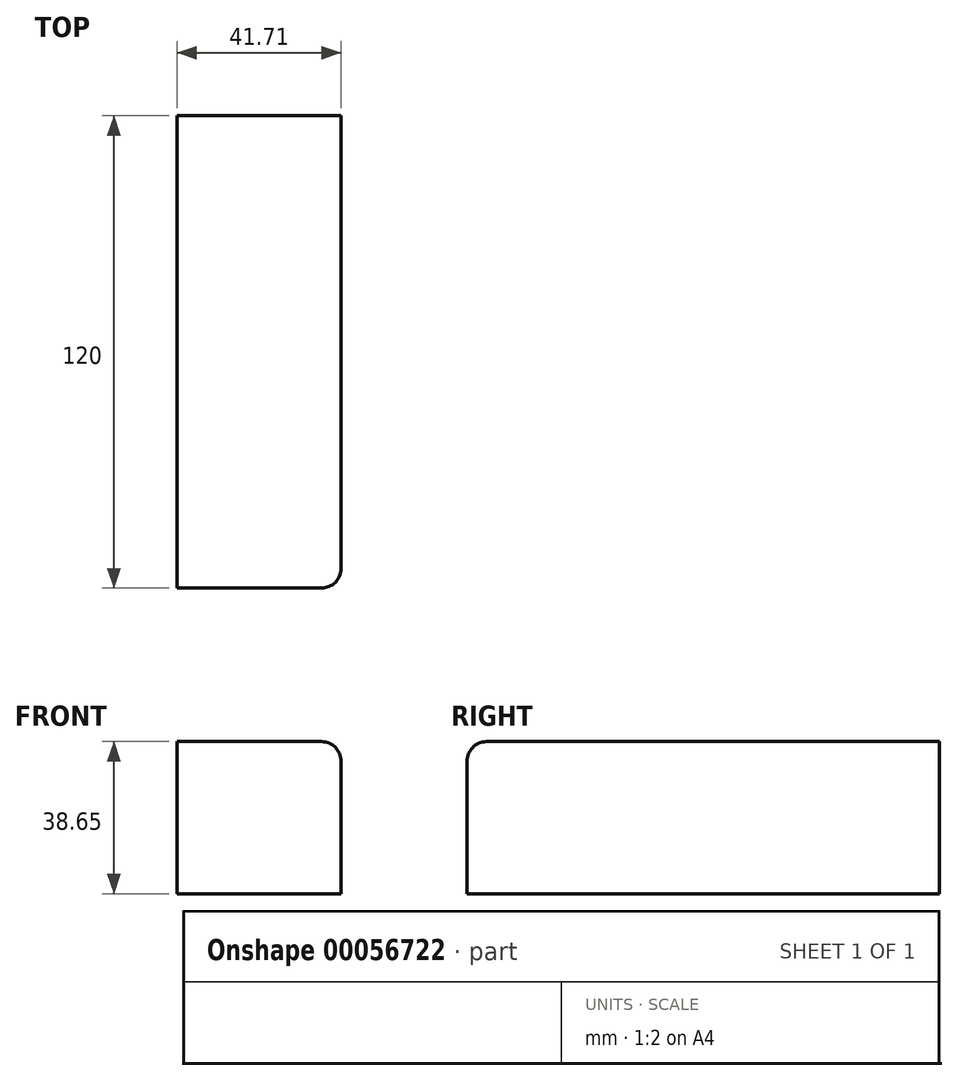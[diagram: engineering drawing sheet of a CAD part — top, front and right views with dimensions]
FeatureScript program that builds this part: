
annotation { "Feature Type Name" : "Feature", "Feature Type Description" : "" }
export const myFeature = defineFeature(function(context is Context, id is Id, definition is map)
    precondition{}
    {
        {
            var Q0;
            Q0=qCreatedBy(makeId("Front.planeOp"),FACE);
            var sketch = newSketch(context, id + "F0", { "sketchPlane" : qUnion([Q0])});
            skLineSegment(sketch, "E0.bottom", {"start": v(0, 0) * mm, "end": v(41.71, 0) * mm});
            skLineSegment(sketch, "E0.top", {"start": v(0, 38.65) * mm, "end": v(41.71, 38.65) * mm});
            skLineSegment(sketch, "E0.left", {"start": v(0, 0) * mm, "end": v(0, 38.65) * mm});
            skLineSegment(sketch, "E0.right", {"start": v(41.71, 0) * mm, "end": v(41.71, 38.65) * mm});
            skSolve(sketch);
        }
        {
            var Q0;
            Q0=makeQuery(id+"F0.imprint","IMPRINT",FACE,{"disambiguationData":[TD([[makeQuery(id+"F0.imprint","IMPRINT",EDGE,{"derivedFrom":sQuery(id+"F0.wireOp",EDGE,"E0.bottom")}),1.0]])]});
            extrude(context, id + "F1", {"entities" : qUnion([Q0]), "depth" : 120 * mm});
        }
        {
            var Q0;
            Q0=makeQuery(id+"F1.opExtrude","SWEPT_EDGE",EDGE,{"disambiguationData":[OSD([sQuery(id+"F0.wireOp",EDGE,"E0.top"),sQuery(id+"F0.wireOp",EDGE,"E0.right")])]});
            var Q1;
            Q1=makeQuery(id+"F1.opExtrude","CAP_EDGE",EDGE,{"disambiguationData":[OSD([sQuery(id+"F0.wireOp",EDGE,"E0.top")])],"isStart":false});
            var Q2;
            Q2=makeQuery(id+"F1.opExtrude","CAP_EDGE",EDGE,{"disambiguationData":[OSD([sQuery(id+"F0.wireOp",EDGE,"E0.right")])],"isStart":false});
            fillet(context, id + "F2", {"entities" : qUnion([Q0, Q1, Q2]), "radius" : 5 * mm, "tangentPropagation" : true, "allowEdgeOverflow" : false});
        }
    });
